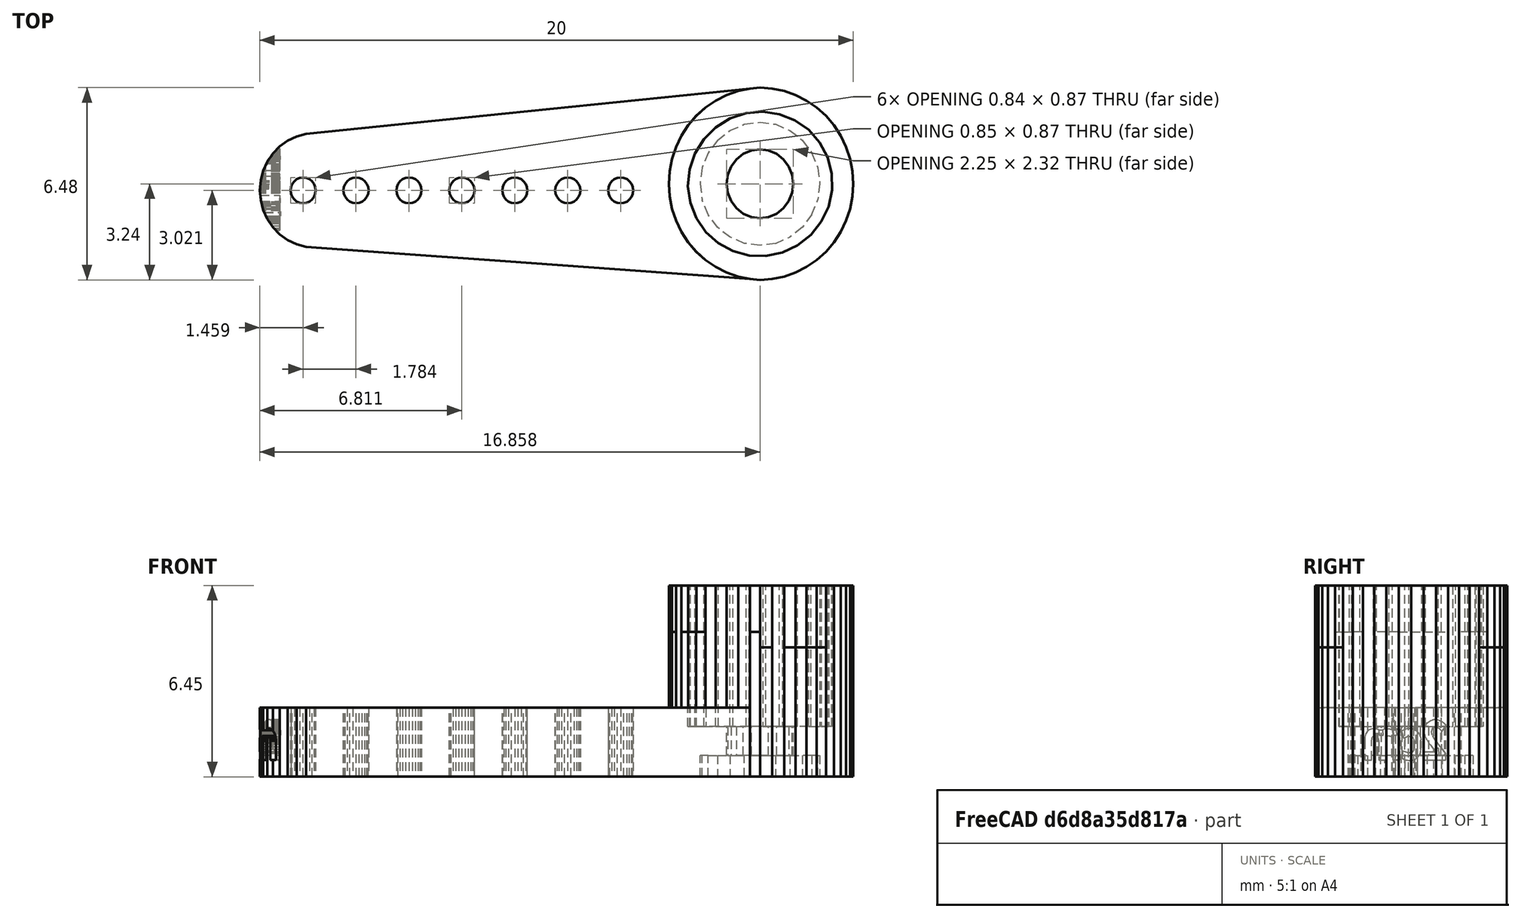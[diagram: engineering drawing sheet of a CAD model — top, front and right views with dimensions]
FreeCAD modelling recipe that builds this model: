
FCSTD DOCUMENT  (FreeCAD 0.20R29177 +426 (Git))
Label: refinedHorn
License: All rights reserved
LicenseURL: http://en.wikipedia.org/wiki/All_rights_reserved
objects: Part::Feature×2, PartDesign::CoordinateSystem×2, Mesh::Feature×1, Part::Refine×1, PartDesign::FeatureBase×1, Sketcher::SketchObject×1, PartDesign::Body×1
note: 8 computed .brp shape members not serialized (recipe doc carries the construction recipe); baked Part::Feature solids carry a one-line shape summary decoded from their .brp

FEATURE [Mesh::Feature] _0mm_servoHorn  label="20mm-servoHorn"
FEATURE [Part::Feature] _0mm_servoHorn001
  shape: bbox 20 x 6.479 x 6.445 mm, 2350 faces, 0 solids (baked)
FEATURE [Part::Refine] _0mm_servoHorn001001
  Source = -> _0mm_servoHorn001
FEATURE [Part::Feature] _0mm_servoHorn001001_solid  label="_0mm_servoHorn001001 (Solid)"
  shape: bbox 20 x 6.479 x 6.445 mm, 888 faces (baked)
FEATURE [PartDesign::FeatureBase] BaseFeature
  BaseFeature = -> _0mm_servoHorn001001_solid
FEATURE [PartDesign::CoordinateSystem] LCS_1
  AttacherType = Attacher::AttachEngine3D
  AttachmentOffset = pos=(0,0,0) rot=(0.382683,0.92388,0;3.14159rad)
  MapMode = 45
  Placement = pos=(-80.5131,-325.745,1.691) rot=(-0.686181,0.727431,0;3.14159rad)
  Support = -> [BaseFeature]
FEATURE [Sketcher::SketchObject] Sketch
  ExternalGeometry = -> [BaseFeature]
  FullyConstrained = true
  MapMode = 5
  Placement = pos=(0,0,0.002) rot=(1,0,0;3.14159rad)
  Support = -> [BaseFeature]
  sketch-geometry (5):
    g0: Circle CenterX=-95.4317 CenterY=325.96 CenterZ=0 NormalX=0 NormalY=0 NormalZ=1 AngleXU=0 Radius=1.94454
    g1: Circle CenterX=-80.6171 CenterY=325.74 CenterZ=0 NormalX=0 NormalY=0 NormalZ=1 AngleXU=0 Radius=3.24089
    g2: Circle CenterX=-95.9081 CenterY=325.959 CenterZ=0 NormalX=0 NormalY=0 NormalZ=1 AngleXU=0 Radius=0.435168
    g3: Circle CenterX=-92.3401 CenterY=325.959 CenterZ=0 NormalX=0 NormalY=0 NormalZ=1 AngleXU=0 Radius=0.435168
    g4: Circle CenterX=-88.7721 CenterY=325.959 CenterZ=0 NormalX=0 NormalY=0 NormalZ=1 AngleXU=0 Radius=0.435168
  constraints (21):
    c: PointOnObject(g-10,g0)
    c: PointOnObject(g-11,g0)
    c: PointOnObject(g-9,g0)
    c: PointOnObject(g-6,g1)
    c: PointOnObject(g-8,g1)
    c: PointOnObject(g-7,g1)
    c: Diameter(g1) = 6.48178
    c: Diameter(g0) = 3.88909
    c: DistanceX(g0,g1) = 14.8146
    c: PointOnObject(g-12,g2)
    c: PointOnObject(g-14,g2)
    c: PointOnObject(g-13,g2)
    c: PointOnObject(g-15,g3)
    c: PointOnObject(g-17,g3)
    c: PointOnObject(g-16,g3)
    c: DistanceX(g2,g3) = 3.568
    c: DistanceX(g-9,g2) = 1.46816
    c: PointOnObject(g-19,g4)
    c: PointOnObject(g-20,g4)
    c: PointOnObject(g-18,g4)
    c: DistanceX(g3,g4) = 3.568
FEATURE [PartDesign::CoordinateSystem] hexagonPlacement_LCS
  AttacherType = Attacher::AttachEngine3D
  AttachmentOffset = pos=(0,0,0) rot=(0,1,0;3.14159rad)
  MapMode = 45
  Placement = pos=(-87.3366,-325.835,0.002) rot=(-0.712245,0.701931,0;3.14159rad)
  Support = -> [BaseFeature]
FEATURE [PartDesign::Body] Body  label="HornBody"
  BaseFeature = -> _0mm_servoHorn001001_solid
  Group = -> [BaseFeature,LCS_1,Sketch,hexagonPlacement_LCS]
  Origin = -> Origin
  Tip = -> BaseFeature
